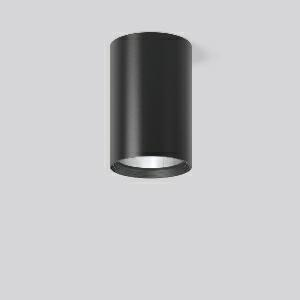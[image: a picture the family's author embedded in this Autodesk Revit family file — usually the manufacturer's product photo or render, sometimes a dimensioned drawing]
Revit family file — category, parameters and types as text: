
# Revit family: heledon_maxi_a_931237_003_76_029f
name_source: partatom
category: Lighting Fixtures
units: mm (PartAtom-declared; Revit-internal decimal feet)

## family parameters
Cut with Voids When Loaded = No
Host = Face
Light Source = No
Part Type = Normal
Room Calculation Point = No
Round Connector Dimension = Use Diameter
Shared = No

## types (1)
- HELEDON maxi A (1 x LED Modul 920 meat+, 2200 lm, 2000)
    Apparent Load = 33 VA
    Approval mark = CE
    CIE Flux Codes = 100 100 100 100 100
    Color Rendering = 90
    Color Temperature = 2000
    Default Elevation = 1800 mm
    Description = Series: HELEDON maxi
Cylindrical surface-mounted downlight. Housing: die-cast aluminium, powder-coated. Internal ceiling frame polycarbonate with bayonet mounting. Black plastic ring and recessed LED to prevent glare from the side. Optical assembly with reflector made of MIRO-Silver with 98% total light reflection for outstanding efficiency - can be changed without tools. Special LED for illumination of meat included. Suitable for Ceiling mounting. Easy installation with a separate ceiling frame with bayonet mounting and plug connection. Driver integrated. Connected via plug-in connector. High quality converter without flickering and stroboscopic effect. The following accessories can be mounted without use of tools: interchangeable lenses, decorative glasses, honeycomb louvre, clear and frosted diffusers, white interchangeable plastic ring. 
Colour: deep black, matt (RAL 9005)
Diameter: 123 mm
Height: 183 mm
Lamp: LED
Socket: without socket
Colour temperature: meat +
System power: 33 W
Rated luminous flux: 2200 lm
Luminous efficiency: 67 lm/W
Control gear: Converter, dimmable, DALI
Protection class: I
Type of protection: IP 20
    Height = 183 mm
    Lamp = 1 x LED Modul 920 meat+
    Lamp Light Flux = 2200 lm
    Lamp count = 1
    Length = 123 mm
    Lifetime = 50000 h
    Luminous efficacy = 67 lm/W
    Manufacturer = RZB
    ModVariant = No
    Model = 931237.003.76
    Mounting Place = Ceiling
    Mounting Type = Surface mounted
    Number of Poles = 1
    OnlyDefault = Yes
    Power Factor = 1
    Product Name = HELEDON maxi A
    Product group = Surface mounted downlights
    ProductGroupID = 302
    Protection Class = Protection class I
    Protection Degree = IP 20
    RLX_Detail_Level = 1
    RLX_Emergency_Light_Flux = 0 lm
    RLX_Emergency_Type = 0
    RLX_Emergency_Type_DB = No
    RlxData = <blob elided: 98113 chars, md5=41b214b6>
    Socket = socket
    Standby Power = 0 W
    System Light Flux = 2200 lm
    System Power = 33 W
    Type Comments = Product without accessories
    Type Image = 931192.003.jpg
    URL = http://relux.com
    VarID = ---
    Voltage = 230 V
    Voltage Range = 220-240 V
    Weight = 0.00 kg
    Width = 0 mm  [stored 0 ft]

note: [stored X ft] marks values corroborated as IEEE doubles in the binary element streams (Revit-internal decimal feet)

## geometry (parser evidence)
native form markers: Blend x4, Sweep x11
no freeform markers — native parametric forms only
